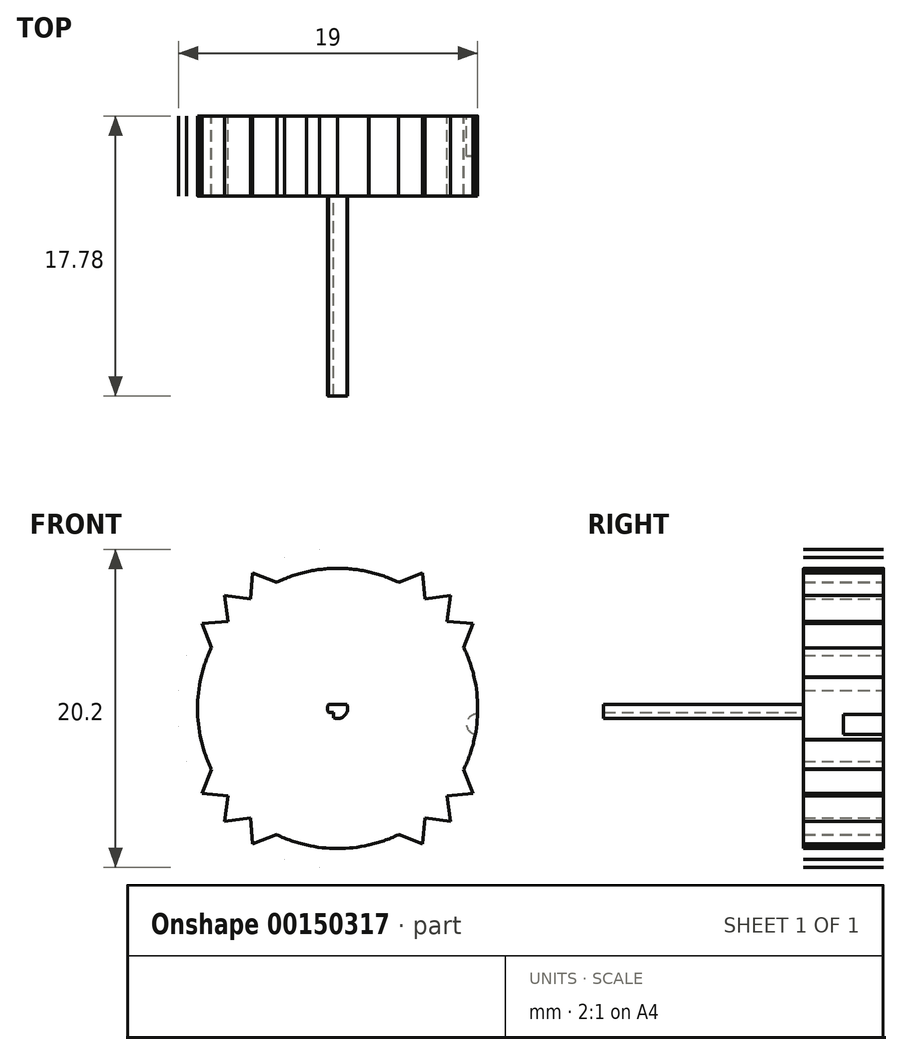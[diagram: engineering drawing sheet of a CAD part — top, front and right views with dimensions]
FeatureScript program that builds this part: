
annotation { "Feature Type Name" : "Feature", "Feature Type Description" : "" }
export const myFeature = defineFeature(function(context is Context, id is Id, definition is map)
    precondition{}
    {
        {
            var Q0;
            Q0=qCreatedBy(makeId("Front.planeOp"),FACE);
            var sketch = newSketch(context, id + "F0", { "sketchPlane" : qUnion([Q0])});
            skCircle(sketch, "E0", {"center": v(0, 0) * mm, "radius": 10.16 * mm});
            skCircle(sketch, "E1", {"center": v(0, 0) * mm, "radius": 8.9 * mm});
            skLineSegment(sketch, "E2", {"start": v(0, 0) * mm, "end": v(0, 8.9) * mm});
            skLineSegment(sketch, "E3", {"start": v(0, 8.9) * mm, "end": v(0, -8.9) * mm});
            skLineSegment(sketch, "E4", {"start": v(0, -8.9) * mm, "end": v(-1.14, -10.1) * mm});
            skLineSegment(sketch, "E5", {"start": v(-1.14, -10.1) * mm, "end": v(-1.98, -8.67) * mm});
            skLineSegment(sketch, "E6", {"start": v(-1.98, -8.67) * mm, "end": v(0, 0) * mm});
            skLineSegment(sketch, "E7", {"start": v(-1.14, -10.1) * mm, "end": v(0, 0) * mm});
            skLineSegment(sketch, "E8", {"start": v(0, 0) * mm, "end": v(-3.36, -9.59) * mm});
            skLineSegment(sketch, "E9", {"start": v(0, 0) * mm, "end": v(-3.86, -8) * mm});
            skLineSegment(sketch, "E10", {"start": v(-3.86, -8) * mm, "end": v(-3.36, -9.59) * mm});
            skLineSegment(sketch, "E11", {"start": v(-1.98, -8.67) * mm, "end": v(-3.36, -9.59) * mm});
            skLineSegment(sketch, "E12.MirrorCS", {"start": v(-3.86, -8) * mm, "end": v(-5.4, -8.6) * mm});
            skLineSegment(sketch, "E13.MirrorCS", {"start": v(0, 0) * mm, "end": v(-5.4, -8.6) * mm});
            skLineSegment(sketch, "E14.MirrorCS", {"start": v(-5.54, -6.95) * mm, "end": v(-5.4, -8.6) * mm});
            skLineSegment(sketch, "E15.MirrorCS", {"start": v(-7.18, -7.18) * mm, "end": v(-5.54, -6.95) * mm});
            skLineSegment(sketch, "E16.MirrorCS", {"start": v(-5.54, -6.95) * mm, "end": v(0, 0) * mm});
            skLineSegment(sketch, "E17.MirrorCS", {"start": v(-7.18, -7.18) * mm, "end": v(0, 0) * mm});
            skLineSegment(sketch, "E18.MirrorCS", {"start": v(-6.95, -5.54) * mm, "end": v(-7.18, -7.18) * mm});
            skLineSegment(sketch, "E19.MirrorCS", {"start": v(6.95, 5.54) * mm, "end": v(-6.95, -5.54) * mm});
            skLineSegment(sketch, "E20.MirrorCS", {"start": v(-6.95, -5.54) * mm, "end": v(-8.6, -5.4) * mm});
            skLineSegment(sketch, "E21.MirrorCS", {"start": v(-8.6, -5.4) * mm, "end": v(0, 0) * mm});
            skLineSegment(sketch, "E22.MirrorCS", {"start": v(-8.6, -5.4) * mm, "end": v(-8, -3.86) * mm});
            skLineSegment(sketch, "E23.MirrorCS", {"start": v(-8, -3.86) * mm, "end": v(0, 0) * mm});
            skLineSegment(sketch, "E24.MirrorCS", {"start": v(-8, -3.86) * mm, "end": v(-9.59, -3.36) * mm});
            skLineSegment(sketch, "E25.MirrorCS", {"start": v(0, 0) * mm, "end": v(-9.59, -3.36) * mm});
            skLineSegment(sketch, "E26.MirrorCS", {"start": v(-8.67, -1.98) * mm, "end": v(-9.59, -3.36) * mm});
            skLineSegment(sketch, "E27.MirrorCS", {"start": v(0, 0) * mm, "end": v(-8.67, -1.98) * mm});
            skLineSegment(sketch, "E28.MirrorCS", {"start": v(-8.67, -1.98) * mm, "end": v(-10.1, -1.14) * mm});
            skLineSegment(sketch, "E29.MirrorCS", {"start": v(0, 0) * mm, "end": v(-10.1, -1.14) * mm});
            skLineSegment(sketch, "E30.MirrorCS", {"start": v(-8.9, 0) * mm, "end": v(-10.1, -1.14) * mm});
            skLineSegment(sketch, "E31.MirrorCS", {"start": v(-8.9, 0) * mm, "end": v(0, 0) * mm});
            skLineSegment(sketch, "E32.MirrorCS", {"start": v(-10.1, 1.14) * mm, "end": v(-8.9, 0) * mm});
            skLineSegment(sketch, "E33.MirrorCS", {"start": v(-10.1, 1.14) * mm, "end": v(0, 0) * mm});
            skLineSegment(sketch, "E34.MirrorCS", {"start": v(-8.67, 1.98) * mm, "end": v(-10.1, 1.14) * mm});
            skLineSegment(sketch, "E35.MirrorCS", {"start": v(8.67, -1.98) * mm, "end": v(-8.67, 1.98) * mm});
            skLineSegment(sketch, "E36.MirrorCS", {"start": v(-8.67, 1.98) * mm, "end": v(-9.59, 3.36) * mm});
            skLineSegment(sketch, "E37.MirrorCS", {"start": v(-9.59, 3.36) * mm, "end": v(0, 0) * mm});
            skLineSegment(sketch, "E38.MirrorCS", {"start": v(-9.59, 3.36) * mm, "end": v(-8, 3.86) * mm});
            skLineSegment(sketch, "E39.MirrorCS", {"start": v(-8, 3.86) * mm, "end": v(0, 0) * mm});
            skLineSegment(sketch, "E40.MirrorCS", {"start": v(-8, 3.86) * mm, "end": v(-8.6, 5.4) * mm});
            skLineSegment(sketch, "E41.MirrorCS", {"start": v(0, 0) * mm, "end": v(-8.6, 5.4) * mm});
            skLineSegment(sketch, "E42.MirrorCS", {"start": v(-6.95, 5.54) * mm, "end": v(-8.6, 5.4) * mm});
            skLineSegment(sketch, "E43.MirrorCS", {"start": v(0, 0) * mm, "end": v(-6.95, 5.54) * mm});
            skLineSegment(sketch, "E44.MirrorCS", {"start": v(-6.95, 5.54) * mm, "end": v(-7.18, 7.18) * mm});
            skLineSegment(sketch, "E45.MirrorCS", {"start": v(0, 0) * mm, "end": v(-7.18, 7.18) * mm});
            skLineSegment(sketch, "E46.MirrorCS", {"start": v(-5.54, 6.95) * mm, "end": v(-7.18, 7.18) * mm});
            skLineSegment(sketch, "E47.MirrorCS", {"start": v(-5.54, 6.95) * mm, "end": v(0, 0) * mm});
            skLineSegment(sketch, "E48.MirrorCS", {"start": v(-5.4, 8.6) * mm, "end": v(-5.54, 6.95) * mm});
            skLineSegment(sketch, "E49.MirrorCS", {"start": v(-5.4, 8.6) * mm, "end": v(0, 0) * mm});
            skLineSegment(sketch, "E50.MirrorCS", {"start": v(-3.86, 8) * mm, "end": v(-5.4, 8.6) * mm});
            skLineSegment(sketch, "E51.MirrorCS", {"start": v(3.86, -8) * mm, "end": v(-3.86, 8) * mm});
            skLineSegment(sketch, "E52.MirrorCS", {"start": v(-3.86, 8) * mm, "end": v(-3.36, 9.59) * mm});
            skLineSegment(sketch, "E53.MirrorCS", {"start": v(-3.36, 9.59) * mm, "end": v(0, 0) * mm});
            skLineSegment(sketch, "E54.MirrorCS", {"start": v(-3.36, 9.59) * mm, "end": v(-1.98, 8.67) * mm});
            skLineSegment(sketch, "E55.MirrorCS", {"start": v(-1.98, 8.67) * mm, "end": v(0, 0) * mm});
            skLineSegment(sketch, "E56.MirrorCS", {"start": v(-1.98, 8.67) * mm, "end": v(-1.14, 10.1) * mm});
            skLineSegment(sketch, "E57.MirrorCS", {"start": v(0, 0) * mm, "end": v(-1.14, 10.1) * mm});
            skLineSegment(sketch, "E58.MirrorCS", {"start": v(0, 8.89) * mm, "end": v(-1.14, 10.1) * mm});
            skLineSegment(sketch, "E59.MirrorCS", {"start": v(0, 0) * mm, "end": v(0, 8.89) * mm});
            skLineSegment(sketch, "E60.MirrorCS", {"start": v(0, 8.89) * mm, "end": v(1.14, 10.1) * mm});
            skLineSegment(sketch, "E61.MirrorCS", {"start": v(0, 0) * mm, "end": v(1.14, 10.1) * mm});
            skLineSegment(sketch, "E62.MirrorCS", {"start": v(1.98, 8.67) * mm, "end": v(1.14, 10.1) * mm});
            skLineSegment(sketch, "E63.MirrorCS", {"start": v(1.98, 8.67) * mm, "end": v(0, 0) * mm});
            skLineSegment(sketch, "E64.MirrorCS", {"start": v(3.36, 9.59) * mm, "end": v(1.98, 8.67) * mm});
            skLineSegment(sketch, "E65.MirrorCS", {"start": v(3.36, 9.59) * mm, "end": v(0, 0) * mm});
            skLineSegment(sketch, "E66.MirrorCS", {"start": v(3.86, 8) * mm, "end": v(3.36, 9.59) * mm});
            skLineSegment(sketch, "E67.MirrorCS", {"start": v(-3.86, -8) * mm, "end": v(3.86, 8) * mm});
            skLineSegment(sketch, "E68.MirrorCS", {"start": v(3.86, 8) * mm, "end": v(5.4, 8.6) * mm});
            skLineSegment(sketch, "E69.MirrorCS", {"start": v(5.4, 8.6) * mm, "end": v(0, 0) * mm});
            skLineSegment(sketch, "E70.MirrorCS", {"start": v(5.4, 8.6) * mm, "end": v(5.54, 6.95) * mm});
            skLineSegment(sketch, "E71.MirrorCS", {"start": v(5.54, 6.95) * mm, "end": v(0, 0) * mm});
            skLineSegment(sketch, "E72.MirrorCS", {"start": v(5.54, 6.95) * mm, "end": v(7.18, 7.18) * mm});
            skLineSegment(sketch, "E73.MirrorCS", {"start": v(0, 0) * mm, "end": v(7.18, 7.18) * mm});
            skLineSegment(sketch, "E74.MirrorCS", {"start": v(6.95, 5.54) * mm, "end": v(7.18, 7.18) * mm});
            skLineSegment(sketch, "E75.MirrorCS", {"start": v(6.95, 5.54) * mm, "end": v(8.6, 5.4) * mm});
            skLineSegment(sketch, "E76.MirrorCS", {"start": v(0, 0) * mm, "end": v(8.6, 5.4) * mm});
            skLineSegment(sketch, "E77.MirrorCS", {"start": v(8, 3.86) * mm, "end": v(8.6, 5.4) * mm});
            skLineSegment(sketch, "E78.MirrorCS", {"start": v(8, 3.86) * mm, "end": v(0, 0) * mm});
            skLineSegment(sketch, "E79.MirrorCS", {"start": v(9.59, 3.36) * mm, "end": v(8, 3.86) * mm});
            skLineSegment(sketch, "E80.MirrorCS", {"start": v(9.59, 3.36) * mm, "end": v(0, 0) * mm});
            skLineSegment(sketch, "E81.MirrorCS", {"start": v(8.67, 1.98) * mm, "end": v(9.59, 3.36) * mm});
            skLineSegment(sketch, "E82.MirrorCS", {"start": v(-8.67, -1.98) * mm, "end": v(8.67, 1.98) * mm});
            skLineSegment(sketch, "E83.MirrorCS", {"start": v(8.67, 1.98) * mm, "end": v(10.1, 1.14) * mm});
            skLineSegment(sketch, "E84.MirrorCS", {"start": v(10.1, 1.14) * mm, "end": v(8.9, 0) * mm});
            skLineSegment(sketch, "E85.MirrorCS", {"start": v(10.1, 1.14) * mm, "end": v(0, 0) * mm});
            skLineSegment(sketch, "E86.MirrorCS", {"start": v(8.9, 0) * mm, "end": v(0, 0) * mm});
            skLineSegment(sketch, "E87.MirrorCS", {"start": v(8.9, 0) * mm, "end": v(10.1, -1.14) * mm});
            skLineSegment(sketch, "E88.MirrorCS", {"start": v(0, 0) * mm, "end": v(10.1, -1.14) * mm});
            skLineSegment(sketch, "E89.MirrorCS", {"start": v(8.67, -1.98) * mm, "end": v(10.1, -1.14) * mm});
            skLineSegment(sketch, "E90.MirrorCS", {"start": v(0, 0) * mm, "end": v(8.67, -1.98) * mm});
            skLineSegment(sketch, "E91.MirrorCS", {"start": v(8.67, -1.98) * mm, "end": v(9.59, -3.36) * mm});
            skLineSegment(sketch, "E92.MirrorCS", {"start": v(0, 0) * mm, "end": v(9.59, -3.36) * mm});
            skLineSegment(sketch, "E93.MirrorCS", {"start": v(8, -3.86) * mm, "end": v(9.59, -3.36) * mm});
            skLineSegment(sketch, "E94.MirrorCS", {"start": v(8, -3.86) * mm, "end": v(0, 0) * mm});
            skLineSegment(sketch, "E95.MirrorCS", {"start": v(8.6, -5.4) * mm, "end": v(8, -3.86) * mm});
            skLineSegment(sketch, "E96.MirrorCS", {"start": v(8.6, -5.4) * mm, "end": v(0, 0) * mm});
            skLineSegment(sketch, "E97.MirrorCS", {"start": v(6.95, -5.54) * mm, "end": v(8.6, -5.4) * mm});
            skLineSegment(sketch, "E98.MirrorCS", {"start": v(-6.95, 5.54) * mm, "end": v(6.95, -5.54) * mm});
            skLineSegment(sketch, "E99.MirrorCS", {"start": v(6.95, -5.54) * mm, "end": v(7.18, -7.18) * mm});
            skLineSegment(sketch, "E100.MirrorCS", {"start": v(7.18, -7.18) * mm, "end": v(0, 0) * mm});
            skLineSegment(sketch, "E101.MirrorCS", {"start": v(7.18, -7.18) * mm, "end": v(5.54, -6.95) * mm});
            skLineSegment(sketch, "E102.MirrorCS", {"start": v(5.54, -6.95) * mm, "end": v(0, 0) * mm});
            skLineSegment(sketch, "E103.MirrorCS", {"start": v(5.54, -6.95) * mm, "end": v(5.4, -8.6) * mm});
            skLineSegment(sketch, "E104.MirrorCS", {"start": v(0, 0) * mm, "end": v(5.4, -8.6) * mm});
            skLineSegment(sketch, "E105.MirrorCS", {"start": v(3.86, -8) * mm, "end": v(5.4, -8.6) * mm});
            skLineSegment(sketch, "E106.MirrorCS", {"start": v(0, 0) * mm, "end": v(3.86, -8) * mm});
            skLineSegment(sketch, "E107.MirrorCS", {"start": v(3.86, -8) * mm, "end": v(3.36, -9.59) * mm});
            skLineSegment(sketch, "E108.MirrorCS", {"start": v(1.98, -8.67) * mm, "end": v(3.36, -9.59) * mm});
            skLineSegment(sketch, "E109.MirrorCS", {"start": v(0, 0) * mm, "end": v(3.36, -9.59) * mm});
            skLineSegment(sketch, "E110.MirrorCS", {"start": v(1.98, -8.67) * mm, "end": v(0, 0) * mm});
            skLineSegment(sketch, "E111.MirrorCS", {"start": v(1.14, -10.1) * mm, "end": v(1.98, -8.67) * mm});
            skLineSegment(sketch, "E112.MirrorCS", {"start": v(1.14, -10.1) * mm, "end": v(0, 0) * mm});
            skLineSegment(sketch, "E113.MirrorCS", {"start": v(0, -8.9) * mm, "end": v(1.14, -10.1) * mm});
            skSolve(sketch);
        }
        {
            var Q0;
            {var subQ0=sQuery(id+"F0.wireOp",EDGE,"E51.MirrorCS");Q0=makeQuery(id+"F0.imprint","IMPRINT",FACE,{"disambiguationData":[TD([[makeQuery(id+"F0.imprint","IMPRINT",EDGE,{"derivedFrom":subQ0}),1.0]])]});}
            var Q1;
            {var subQ0=sQuery(id+"F0.wireOp",EDGE,"E47.MirrorCS");Q1=makeQuery(id+"F0.imprint","IMPRINT",FACE,{"disambiguationData":[TD([[makeQuery(id+"F0.imprint","IMPRINT",EDGE,{"derivedFrom":subQ0}),1.0]])]});}
            var Q2;
            {var subQ0=sQuery(id+"F0.wireOp",EDGE,"E48.MirrorCS");Q2=makeQuery(id+"F0.imprint","IMPRINT",FACE,{"disambiguationData":[TD([[makeQuery(id+"F0.imprint","IMPRINT",EDGE,{"derivedFrom":subQ0}),1.0]])]});}
            var Q3;
            {var subQ0=sQuery(id+"F0.wireOp",EDGE,"E50.MirrorCS");Q3=makeQuery(id+"F0.imprint","IMPRINT",FACE,{"disambiguationData":[TD([[makeQuery(id+"F0.imprint","IMPRINT",EDGE,{"derivedFrom":subQ0}),1.0]])]});}
            var Q4;
            {var subQ0=sQuery(id+"F0.wireOp",EDGE,"E52.MirrorCS");Q4=makeQuery(id+"F0.imprint","IMPRINT",FACE,{"disambiguationData":[TD([[makeQuery(id+"F0.imprint","IMPRINT",EDGE,{"derivedFrom":subQ0}),-1.0]])]});}
            var Q5;
            {var subQ0=sQuery(id+"F0.wireOp",EDGE,"E54.MirrorCS");Q5=makeQuery(id+"F0.imprint","IMPRINT",FACE,{"disambiguationData":[TD([[makeQuery(id+"F0.imprint","IMPRINT",EDGE,{"derivedFrom":subQ0}),-1.0]])]});}
            var Q6;
            {var subQ0=sQuery(id+"F0.wireOp",EDGE,"E55.MirrorCS");Q6=makeQuery(id+"F0.imprint","IMPRINT",FACE,{"disambiguationData":[TD([[makeQuery(id+"F0.imprint","IMPRINT",EDGE,{"derivedFrom":subQ0}),-1.0]])]});}
            var Q7;
            {var subQ0=sQuery(id+"F0.wireOp",EDGE,"E51.MirrorCS");Q7=makeQuery(id+"F0.imprint","IMPRINT",FACE,{"disambiguationData":[TD([[makeQuery(id+"F0.imprint","IMPRINT",EDGE,{"derivedFrom":subQ0}),-1.0]])]});}
            var Q8;
            {var subQ1=sQuery(id+"F0.wireOp",EDGE,"E1");var subQ3=sQuery(id+"F0.wireOp",EDGE,"E57.MirrorCS");var subQ4=makeQuery(id+"F0.imprint","INTERSECT",VERTEX,{"derivedFrom":[subQ1,subQ3]});Q8=makeQuery(id+"F0.imprint","IMPRINT",FACE,{"disambiguationData":[TD([[makeQuery(id+"F0.imprint","IMPRINT",EDGE,{"disambiguationData":[TD([[subQ4,1.0]])],"derivedFrom":subQ1}),1.0]])]});}
            var Q9;
            {var subQ0=sQuery(id+"F0.wireOp",EDGE,"E58.MirrorCS");Q9=makeQuery(id+"F0.imprint","IMPRINT",FACE,{"disambiguationData":[TD([[makeQuery(id+"F0.imprint","IMPRINT",EDGE,{"derivedFrom":subQ0}),1.0]])]});}
            var Q10;
            {var subQ0=sQuery(id+"F0.wireOp",EDGE,"E56.MirrorCS");Q10=makeQuery(id+"F0.imprint","IMPRINT",FACE,{"disambiguationData":[TD([[makeQuery(id+"F0.imprint","IMPRINT",EDGE,{"derivedFrom":subQ0}),-1.0]])]});}
            var Q11;
            {var subQ0=sQuery(id+"F0.wireOp",EDGE,"E55.MirrorCS");Q11=makeQuery(id+"F0.imprint","IMPRINT",FACE,{"disambiguationData":[TD([[makeQuery(id+"F0.imprint","IMPRINT",EDGE,{"derivedFrom":subQ0}),1.0]])]});}
            var Q12;
            {var subQ0=sQuery(id+"F0.wireOp",EDGE,"E47.MirrorCS");Q12=makeQuery(id+"F0.imprint","IMPRINT",FACE,{"disambiguationData":[TD([[makeQuery(id+"F0.imprint","IMPRINT",EDGE,{"derivedFrom":subQ0}),-1.0]])]});}
            var Q13;
            {var subQ0=sQuery(id+"F0.wireOp",EDGE,"E46.MirrorCS");Q13=makeQuery(id+"F0.imprint","IMPRINT",FACE,{"disambiguationData":[TD([[makeQuery(id+"F0.imprint","IMPRINT",EDGE,{"derivedFrom":subQ0}),1.0]])]});}
            var Q14;
            {var subQ1=sQuery(id+"F0.wireOp",EDGE,"E1");var subQ3=sQuery(id+"F0.wireOp",EDGE,"E45.MirrorCS");var subQ4=makeQuery(id+"F0.imprint","INTERSECT",VERTEX,{"derivedFrom":[subQ1,subQ3]});Q14=makeQuery(id+"F0.imprint","IMPRINT",FACE,{"disambiguationData":[TD([[makeQuery(id+"F0.imprint","IMPRINT",EDGE,{"disambiguationData":[TD([[subQ4,-1.0]])],"derivedFrom":subQ1}),1.0]])]});}
            var Q15;
            {var subQ0=sQuery(id+"F0.wireOp",EDGE,"E44.MirrorCS");Q15=makeQuery(id+"F0.imprint","IMPRINT",FACE,{"disambiguationData":[TD([[makeQuery(id+"F0.imprint","IMPRINT",EDGE,{"derivedFrom":subQ0}),-1.0]])]});}
            var Q16;
            {var subQ1=sQuery(id+"F0.wireOp",EDGE,"E1");var subQ3=sQuery(id+"F0.wireOp",EDGE,"E41.MirrorCS");var subQ4=makeQuery(id+"F0.imprint","INTERSECT",VERTEX,{"derivedFrom":[subQ1,subQ3]});Q16=makeQuery(id+"F0.imprint","IMPRINT",FACE,{"disambiguationData":[TD([[makeQuery(id+"F0.imprint","IMPRINT",EDGE,{"disambiguationData":[TD([[subQ4,1.0]])],"derivedFrom":subQ1}),1.0]])]});}
            var Q17;
            {var subQ0=sQuery(id+"F0.wireOp",EDGE,"E42.MirrorCS");Q17=makeQuery(id+"F0.imprint","IMPRINT",FACE,{"disambiguationData":[TD([[makeQuery(id+"F0.imprint","IMPRINT",EDGE,{"derivedFrom":subQ0}),1.0]])]});}
            var Q18;
            {var subQ0=sQuery(id+"F0.wireOp",EDGE,"E40.MirrorCS");Q18=makeQuery(id+"F0.imprint","IMPRINT",FACE,{"disambiguationData":[TD([[makeQuery(id+"F0.imprint","IMPRINT",EDGE,{"derivedFrom":subQ0}),-1.0]])]});}
            var Q19;
            {var subQ0=sQuery(id+"F0.wireOp",EDGE,"E39.MirrorCS");Q19=makeQuery(id+"F0.imprint","IMPRINT",FACE,{"disambiguationData":[TD([[makeQuery(id+"F0.imprint","IMPRINT",EDGE,{"derivedFrom":subQ0}),1.0]])]});}
            var Q20;
            {var subQ0=sQuery(id+"F0.wireOp",EDGE,"E39.MirrorCS");Q20=makeQuery(id+"F0.imprint","IMPRINT",FACE,{"disambiguationData":[TD([[makeQuery(id+"F0.imprint","IMPRINT",EDGE,{"derivedFrom":subQ0}),-1.0]])]});}
            var Q21;
            {var subQ0=sQuery(id+"F0.wireOp",EDGE,"E38.MirrorCS");Q21=makeQuery(id+"F0.imprint","IMPRINT",FACE,{"disambiguationData":[TD([[makeQuery(id+"F0.imprint","IMPRINT",EDGE,{"derivedFrom":subQ0}),-1.0]])]});}
            var Q22;
            {var subQ0=sQuery(id+"F0.wireOp",EDGE,"E36.MirrorCS");Q22=makeQuery(id+"F0.imprint","IMPRINT",FACE,{"disambiguationData":[TD([[makeQuery(id+"F0.imprint","IMPRINT",EDGE,{"derivedFrom":subQ0}),-1.0]])]});}
            var Q23;
            {var subQ0=sQuery(id+"F0.wireOp",EDGE,"E35.MirrorCS");Q23=makeQuery(id+"F0.imprint","IMPRINT",FACE,{"disambiguationData":[TD([[makeQuery(id+"F0.imprint","IMPRINT",EDGE,{"derivedFrom":subQ0}),-1.0]])]});}
            var Q24;
            {var subQ0=sQuery(id+"F0.wireOp",EDGE,"E35.MirrorCS");Q24=makeQuery(id+"F0.imprint","IMPRINT",FACE,{"disambiguationData":[TD([[makeQuery(id+"F0.imprint","IMPRINT",EDGE,{"derivedFrom":subQ0}),1.0]])]});}
            var Q25;
            {var subQ0=sQuery(id+"F0.wireOp",EDGE,"E34.MirrorCS");Q25=makeQuery(id+"F0.imprint","IMPRINT",FACE,{"disambiguationData":[TD([[makeQuery(id+"F0.imprint","IMPRINT",EDGE,{"derivedFrom":subQ0}),1.0]])]});}
            var Q26;
            {var subQ0=sQuery(id+"F0.wireOp",EDGE,"E32.MirrorCS");Q26=makeQuery(id+"F0.imprint","IMPRINT",FACE,{"disambiguationData":[TD([[makeQuery(id+"F0.imprint","IMPRINT",EDGE,{"derivedFrom":subQ0}),1.0]])]});}
            var Q27;
            {var subQ0=sQuery(id+"F0.wireOp",EDGE,"E31.MirrorCS");Q27=makeQuery(id+"F0.imprint","IMPRINT",FACE,{"disambiguationData":[TD([[makeQuery(id+"F0.imprint","IMPRINT",EDGE,{"derivedFrom":subQ0}),1.0]])]});}
            var Q28;
            {var subQ0=sQuery(id+"F0.wireOp",EDGE,"E31.MirrorCS");Q28=makeQuery(id+"F0.imprint","IMPRINT",FACE,{"disambiguationData":[TD([[makeQuery(id+"F0.imprint","IMPRINT",EDGE,{"derivedFrom":subQ0}),-1.0]])]});}
            var Q29;
            {var subQ0=sQuery(id+"F0.wireOp",EDGE,"E30.MirrorCS");Q29=makeQuery(id+"F0.imprint","IMPRINT",FACE,{"disambiguationData":[TD([[makeQuery(id+"F0.imprint","IMPRINT",EDGE,{"derivedFrom":subQ0}),1.0]])]});}
            var Q30;
            {var subQ0=sQuery(id+"F0.wireOp",EDGE,"E28.MirrorCS");Q30=makeQuery(id+"F0.imprint","IMPRINT",FACE,{"disambiguationData":[TD([[makeQuery(id+"F0.imprint","IMPRINT",EDGE,{"derivedFrom":subQ0}),-1.0]])]});}
            var Q31;
            {var subQ1=sQuery(id+"F0.wireOp",EDGE,"E1");var subQ3=sQuery(id+"F0.wireOp",EDGE,"E29.MirrorCS");var subQ4=makeQuery(id+"F0.imprint","INTERSECT",VERTEX,{"derivedFrom":[subQ1,subQ3]});Q31=makeQuery(id+"F0.imprint","IMPRINT",FACE,{"disambiguationData":[TD([[makeQuery(id+"F0.imprint","IMPRINT",EDGE,{"disambiguationData":[TD([[subQ4,-1.0]])],"derivedFrom":subQ1}),1.0]])]});}
            var Q32;
            {var subQ1=sQuery(id+"F0.wireOp",EDGE,"E1");var subQ3=sQuery(id+"F0.wireOp",EDGE,"E25.MirrorCS");var subQ4=makeQuery(id+"F0.imprint","INTERSECT",VERTEX,{"derivedFrom":[subQ1,subQ3]});Q32=makeQuery(id+"F0.imprint","IMPRINT",FACE,{"disambiguationData":[TD([[makeQuery(id+"F0.imprint","IMPRINT",EDGE,{"disambiguationData":[TD([[subQ4,1.0]])],"derivedFrom":subQ1}),1.0]])]});}
            var Q33;
            {var subQ0=sQuery(id+"F0.wireOp",EDGE,"E26.MirrorCS");Q33=makeQuery(id+"F0.imprint","IMPRINT",FACE,{"disambiguationData":[TD([[makeQuery(id+"F0.imprint","IMPRINT",EDGE,{"derivedFrom":subQ0}),1.0]])]});}
            var Q34;
            {var subQ0=sQuery(id+"F0.wireOp",EDGE,"E24.MirrorCS");Q34=makeQuery(id+"F0.imprint","IMPRINT",FACE,{"disambiguationData":[TD([[makeQuery(id+"F0.imprint","IMPRINT",EDGE,{"derivedFrom":subQ0}),-1.0]])]});}
            var Q35;
            {var subQ0=sQuery(id+"F0.wireOp",EDGE,"E23.MirrorCS");Q35=makeQuery(id+"F0.imprint","IMPRINT",FACE,{"disambiguationData":[TD([[makeQuery(id+"F0.imprint","IMPRINT",EDGE,{"derivedFrom":subQ0}),1.0]])]});}
            var Q36;
            {var subQ0=sQuery(id+"F0.wireOp",EDGE,"E23.MirrorCS");Q36=makeQuery(id+"F0.imprint","IMPRINT",FACE,{"disambiguationData":[TD([[makeQuery(id+"F0.imprint","IMPRINT",EDGE,{"derivedFrom":subQ0}),-1.0]])]});}
            var Q37;
            {var subQ0=sQuery(id+"F0.wireOp",EDGE,"E22.MirrorCS");Q37=makeQuery(id+"F0.imprint","IMPRINT",FACE,{"disambiguationData":[TD([[makeQuery(id+"F0.imprint","IMPRINT",EDGE,{"derivedFrom":subQ0}),-1.0]])]});}
            var Q38;
            {var subQ0=sQuery(id+"F0.wireOp",EDGE,"E20.MirrorCS");Q38=makeQuery(id+"F0.imprint","IMPRINT",FACE,{"disambiguationData":[TD([[makeQuery(id+"F0.imprint","IMPRINT",EDGE,{"derivedFrom":subQ0}),-1.0]])]});}
            var Q39;
            {var subQ1=sQuery(id+"F0.wireOp",EDGE,"E1");var subQ3=sQuery(id+"F0.wireOp",EDGE,"E21.MirrorCS");var subQ4=makeQuery(id+"F0.imprint","INTERSECT",VERTEX,{"derivedFrom":[subQ1,subQ3]});Q39=makeQuery(id+"F0.imprint","IMPRINT",FACE,{"disambiguationData":[TD([[makeQuery(id+"F0.imprint","IMPRINT",EDGE,{"disambiguationData":[TD([[subQ4,-1.0]])],"derivedFrom":subQ1}),1.0]])]});}
            var Q40;
            {var subQ1=sQuery(id+"F0.wireOp",EDGE,"E1");var subQ3=sQuery(id+"F0.wireOp",EDGE,"E17.MirrorCS");var subQ4=makeQuery(id+"F0.imprint","INTERSECT",VERTEX,{"derivedFrom":[subQ1,subQ3]});Q40=makeQuery(id+"F0.imprint","IMPRINT",FACE,{"disambiguationData":[TD([[makeQuery(id+"F0.imprint","IMPRINT",EDGE,{"disambiguationData":[TD([[subQ4,1.0]])],"derivedFrom":subQ1}),1.0]])]});}
            var Q41;
            {var subQ0=sQuery(id+"F0.wireOp",EDGE,"E16.MirrorCS");Q41=makeQuery(id+"F0.imprint","IMPRINT",FACE,{"disambiguationData":[TD([[makeQuery(id+"F0.imprint","IMPRINT",EDGE,{"derivedFrom":subQ0}),1.0]])]});}
            var Q42;
            {var subQ0=sQuery(id+"F0.wireOp",EDGE,"E16.MirrorCS");Q42=makeQuery(id+"F0.imprint","IMPRINT",FACE,{"disambiguationData":[TD([[makeQuery(id+"F0.imprint","IMPRINT",EDGE,{"derivedFrom":subQ0}),-1.0]])]});}
            var Q43;
            {var subQ0=sQuery(id+"F0.wireOp",EDGE,"E18.MirrorCS");Q43=makeQuery(id+"F0.imprint","IMPRINT",FACE,{"disambiguationData":[TD([[makeQuery(id+"F0.imprint","IMPRINT",EDGE,{"derivedFrom":subQ0}),1.0]])]});}
            var Q44;
            {var subQ0=sQuery(id+"F0.wireOp",EDGE,"E15.MirrorCS");Q44=makeQuery(id+"F0.imprint","IMPRINT",FACE,{"disambiguationData":[TD([[makeQuery(id+"F0.imprint","IMPRINT",EDGE,{"derivedFrom":subQ0}),1.0]])]});}
            var Q45;
            {var subQ0=sQuery(id+"F0.wireOp",EDGE,"E14.MirrorCS");Q45=makeQuery(id+"F0.imprint","IMPRINT",FACE,{"disambiguationData":[TD([[makeQuery(id+"F0.imprint","IMPRINT",EDGE,{"derivedFrom":subQ0}),1.0]])]});}
            var Q46;
            {var subQ0=sQuery(id+"F0.wireOp",EDGE,"E12.MirrorCS");Q46=makeQuery(id+"F0.imprint","IMPRINT",FACE,{"disambiguationData":[TD([[makeQuery(id+"F0.imprint","IMPRINT",EDGE,{"derivedFrom":subQ0}),-1.0]])]});}
            var Q47;
            {var subQ1=sQuery(id+"F0.wireOp",EDGE,"E1");var subQ3=sQuery(id+"F0.wireOp",EDGE,"E8");var subQ4=makeQuery(id+"F0.imprint","INTERSECT",VERTEX,{"derivedFrom":[subQ1,subQ3]});Q47=makeQuery(id+"F0.imprint","IMPRINT",FACE,{"disambiguationData":[TD([[makeQuery(id+"F0.imprint","IMPRINT",EDGE,{"disambiguationData":[TD([[subQ4,1.0]])],"derivedFrom":subQ1}),1.0]])]});}
            var Q48;
            {var subQ0=sQuery(id+"F0.wireOp",EDGE,"E10");Q48=makeQuery(id+"F0.imprint","IMPRINT",FACE,{"disambiguationData":[TD([[makeQuery(id+"F0.imprint","IMPRINT",EDGE,{"derivedFrom":subQ0}),1.0]])]});}
            var Q49;
            {var subQ0=sQuery(id+"F0.wireOp",EDGE,"E11");Q49=makeQuery(id+"F0.imprint","IMPRINT",FACE,{"disambiguationData":[TD([[makeQuery(id+"F0.imprint","IMPRINT",EDGE,{"derivedFrom":subQ0}),-1.0]])]});}
            var Q50;
            {var subQ0=sQuery(id+"F0.wireOp",EDGE,"E6");Q50=makeQuery(id+"F0.imprint","IMPRINT",FACE,{"disambiguationData":[TD([[makeQuery(id+"F0.imprint","IMPRINT",EDGE,{"derivedFrom":subQ0}),1.0]])]});}
            var Q51;
            {var subQ0=sQuery(id+"F0.wireOp",EDGE,"E6");Q51=makeQuery(id+"F0.imprint","IMPRINT",FACE,{"disambiguationData":[TD([[makeQuery(id+"F0.imprint","IMPRINT",EDGE,{"derivedFrom":subQ0}),-1.0]])]});}
            var Q52;
            {var subQ0=sQuery(id+"F0.wireOp",EDGE,"E4");Q52=makeQuery(id+"F0.imprint","IMPRINT",FACE,{"disambiguationData":[TD([[makeQuery(id+"F0.imprint","IMPRINT",EDGE,{"derivedFrom":subQ0}),-1.0]])]});}
            var Q53;
            {var subQ0=sQuery(id+"F0.wireOp",EDGE,"E5");Q53=makeQuery(id+"F0.imprint","IMPRINT",FACE,{"disambiguationData":[TD([[makeQuery(id+"F0.imprint","IMPRINT",EDGE,{"derivedFrom":subQ0}),-1.0]])]});}
            var Q54;
            {var subQ1=sQuery(id+"F0.wireOp",EDGE,"E1");var subQ3=sQuery(id+"F0.wireOp",EDGE,"E7");var subQ4=makeQuery(id+"F0.imprint","INTERSECT",VERTEX,{"derivedFrom":[subQ1,subQ3]});Q54=makeQuery(id+"F0.imprint","IMPRINT",FACE,{"disambiguationData":[TD([[makeQuery(id+"F0.imprint","IMPRINT",EDGE,{"disambiguationData":[TD([[subQ4,-1.0]])],"derivedFrom":subQ1}),1.0]])]});}
            var Q55;
            {var subQ1=sQuery(id+"F0.wireOp",EDGE,"E1");var subQ3=sQuery(id+"F0.wireOp",EDGE,"E13.MirrorCS");var subQ4=makeQuery(id+"F0.imprint","INTERSECT",VERTEX,{"derivedFrom":[subQ1,subQ3]});Q55=makeQuery(id+"F0.imprint","IMPRINT",FACE,{"disambiguationData":[TD([[makeQuery(id+"F0.imprint","IMPRINT",EDGE,{"disambiguationData":[TD([[subQ4,-1.0]])],"derivedFrom":subQ1}),1.0]])]});}
            extrude(context, id + "F1", {"entities" : qUnion([Q0, Q1, Q2, Q3, Q4, Q5, Q6, Q7, Q8, Q9, Q10, Q11, Q12, Q13, Q14, Q15, Q16, Q17, Q18, Q19, Q20, Q21, Q22, Q23, Q24, Q25, Q26, Q27, Q28, Q29, Q30, Q31, Q32, Q33, Q34, Q35, Q36, Q37, Q38, Q39, Q40, Q41, Q42, Q43, Q44, Q45, Q46, Q47, Q48, Q49, Q50, Q51, Q52, Q53, Q54, Q55]), "depth" : 5.08 * mm});
        }
        {
            var Q0;
            Q0=makeQuery(id+"F1.opExtrude","SWEPT_BODY",BODY,{"disambiguationData":[OSD([sQuery(id+"F0.wireOp",EDGE,"E4"),sQuery(id+"F0.wireOp",EDGE,"E5"),sQuery(id+"F0.wireOp",EDGE,"E10"),sQuery(id+"F0.wireOp",EDGE,"E11"),sQuery(id+"F0.wireOp",EDGE,"E12.MirrorCS"),sQuery(id+"F0.wireOp",EDGE,"E14.MirrorCS"),sQuery(id+"F0.wireOp",EDGE,"E15.MirrorCS"),sQuery(id+"F0.wireOp",EDGE,"E18.MirrorCS"),sQuery(id+"F0.wireOp",EDGE,"E20.MirrorCS"),sQuery(id+"F0.wireOp",EDGE,"E22.MirrorCS"),sQuery(id+"F0.wireOp",EDGE,"E24.MirrorCS"),sQuery(id+"F0.wireOp",EDGE,"E26.MirrorCS"),sQuery(id+"F0.wireOp",EDGE,"E28.MirrorCS"),sQuery(id+"F0.wireOp",EDGE,"E30.MirrorCS"),sQuery(id+"F0.wireOp",EDGE,"E32.MirrorCS"),sQuery(id+"F0.wireOp",EDGE,"E34.MirrorCS"),sQuery(id+"F0.wireOp",EDGE,"E36.MirrorCS"),sQuery(id+"F0.wireOp",EDGE,"E38.MirrorCS"),sQuery(id+"F0.wireOp",EDGE,"E40.MirrorCS"),sQuery(id+"F0.wireOp",EDGE,"E42.MirrorCS"),sQuery(id+"F0.wireOp",EDGE,"E44.MirrorCS"),sQuery(id+"F0.wireOp",EDGE,"E46.MirrorCS"),sQuery(id+"F0.wireOp",EDGE,"E48.MirrorCS"),sQuery(id+"F0.wireOp",EDGE,"E50.MirrorCS"),sQuery(id+"F0.wireOp",EDGE,"E52.MirrorCS"),sQuery(id+"F0.wireOp",EDGE,"E54.MirrorCS"),sQuery(id+"F0.wireOp",EDGE,"E56.MirrorCS"),sQuery(id+"F0.wireOp",EDGE,"E58.MirrorCS"),sQuery(id+"F0.wireOp",EDGE,"E3")])]});
            var Q1;
            Q1=qCreatedBy(makeId("Right.planeOp"),FACE);
            mirror(context, id + "F2", {"operationType" : NewBodyOperationType.ADD, "entities" : qUnion([Q0]), "mirrorPlane" : qUnion([Q1])});
        }
        {
            var Q0;
            {var subQ0=makeQuery(id+"F1.opExtrude","CAP_FACE",FACE,{"disambiguationData":[OSD([sQuery(id+"F0.wireOp",EDGE,"E4"),sQuery(id+"F0.wireOp",EDGE,"E5"),sQuery(id+"F0.wireOp",EDGE,"E10"),sQuery(id+"F0.wireOp",EDGE,"E11"),sQuery(id+"F0.wireOp",EDGE,"E12.MirrorCS"),sQuery(id+"F0.wireOp",EDGE,"E14.MirrorCS"),sQuery(id+"F0.wireOp",EDGE,"E15.MirrorCS"),sQuery(id+"F0.wireOp",EDGE,"E18.MirrorCS"),sQuery(id+"F0.wireOp",EDGE,"E20.MirrorCS"),sQuery(id+"F0.wireOp",EDGE,"E22.MirrorCS"),sQuery(id+"F0.wireOp",EDGE,"E24.MirrorCS"),sQuery(id+"F0.wireOp",EDGE,"E26.MirrorCS"),sQuery(id+"F0.wireOp",EDGE,"E28.MirrorCS"),sQuery(id+"F0.wireOp",EDGE,"E30.MirrorCS"),sQuery(id+"F0.wireOp",EDGE,"E32.MirrorCS"),sQuery(id+"F0.wireOp",EDGE,"E34.MirrorCS"),sQuery(id+"F0.wireOp",EDGE,"E36.MirrorCS"),sQuery(id+"F0.wireOp",EDGE,"E38.MirrorCS"),sQuery(id+"F0.wireOp",EDGE,"E40.MirrorCS"),sQuery(id+"F0.wireOp",EDGE,"E42.MirrorCS"),sQuery(id+"F0.wireOp",EDGE,"E44.MirrorCS"),sQuery(id+"F0.wireOp",EDGE,"E46.MirrorCS"),sQuery(id+"F0.wireOp",EDGE,"E48.MirrorCS"),sQuery(id+"F0.wireOp",EDGE,"E50.MirrorCS"),sQuery(id+"F0.wireOp",EDGE,"E52.MirrorCS"),sQuery(id+"F0.wireOp",EDGE,"E54.MirrorCS"),sQuery(id+"F0.wireOp",EDGE,"E56.MirrorCS"),sQuery(id+"F0.wireOp",EDGE,"E58.MirrorCS"),sQuery(id+"F0.wireOp",EDGE,"E3")])],"isStart":false});Q0=makeQuery(id+"F2.boolean.opBoolean","MERGE",FACE,{"derivedFrom":[subQ0,makeQuery(id+"F2.opPattern","COPY",FACE,{"derivedFrom":subQ0,"instanceName":"1"})]});}
            var sketch = newSketch(context, id + "F3", { "sketchPlane" : qUnion([Q0])});
            skCircle(sketch, "E114", {"center": v(0, 0) * mm, "radius": 0.64 * mm});
            skLineSegment(sketch, "E115.bottom", {"start": v(1.18, 0.25) * mm, "end": v(-1.18, 0.25) * mm});
            skLineSegment(sketch, "E115.top", {"start": v(1.18, -0.25) * mm, "end": v(-1.18, -0.25) * mm});
            skLineSegment(sketch, "E115.left", {"start": v(1.18, 0.25) * mm, "end": v(1.18, -0.25) * mm});
            skLineSegment(sketch, "E115.right", {"start": v(-1.18, 0.25) * mm, "end": v(-1.18, -0.25) * mm});
            skLineSegment(sketch, "E116.bottom", {"start": v(0.25, 1.07) * mm, "end": v(-0.25, 1.07) * mm});
            skLineSegment(sketch, "E116.top", {"start": v(0.25, -1.07) * mm, "end": v(-0.25, -1.07) * mm});
            skLineSegment(sketch, "E116.left", {"start": v(0.25, 1.07) * mm, "end": v(0.25, -1.07) * mm});
            skLineSegment(sketch, "E116.right", {"start": v(-0.25, 1.07) * mm, "end": v(-0.25, -1.07) * mm});
            skSolve(sketch);
        }
        {
            var Q0;
            {var subQ0=sQuery(id+"F3.wireOp",EDGE,"E116.left");var subQ1=sQuery(id+"F3.wireOp",EDGE,"E114");var subQ2=makeQuery(id+"F3.imprint","INTERSECT",VERTEX,{"disambiguationData":[OD(0.0)],"derivedFrom":[subQ1,subQ0]});Q0=makeQuery(id+"F3.imprint","IMPRINT",FACE,{"disambiguationData":[TD([[makeQuery(id+"F3.imprint","IMPRINT",EDGE,{"disambiguationData":[TD([[subQ2,-1.0]])],"derivedFrom":subQ1}),1.0]])]});}
            var Q1;
            {var subQ0=sQuery(id+"F3.wireOp",EDGE,"E115.bottom");var subQ1=sQuery(id+"F3.wireOp",EDGE,"E114");var subQ2=makeQuery(id+"F3.imprint","INTERSECT",VERTEX,{"disambiguationData":[OD(1.0)],"derivedFrom":[subQ1,subQ0]});Q1=makeQuery(id+"F3.imprint","IMPRINT",FACE,{"disambiguationData":[TD([[makeQuery(id+"F3.imprint","IMPRINT",EDGE,{"disambiguationData":[TD([[subQ2,-1.0]])],"derivedFrom":subQ1}),1.0]])]});}
            var Q2;
            {var subQ0=sQuery(id+"F3.wireOp",EDGE,"E116.left");var subQ1=sQuery(id+"F3.wireOp",EDGE,"E115.bottom");var subQ2=makeQuery(id+"F3.imprint","INTERSECT",VERTEX,{"derivedFrom":[subQ1,subQ0]});Q2=makeQuery(id+"F3.imprint","IMPRINT",FACE,{"disambiguationData":[TD([[makeQuery(id+"F3.imprint","IMPRINT",EDGE,{"disambiguationData":[TD([[subQ2,-1.0]])],"derivedFrom":subQ1}),1.0]])]});}
            var Q3;
            {var subQ0=sQuery(id+"F3.wireOp",EDGE,"E115.bottom");var subQ1=sQuery(id+"F3.wireOp",EDGE,"E114");var subQ2=makeQuery(id+"F3.imprint","INTERSECT",VERTEX,{"disambiguationData":[OD(0.0)],"derivedFrom":[subQ1,subQ0]});Q3=makeQuery(id+"F3.imprint","IMPRINT",FACE,{"disambiguationData":[TD([[makeQuery(id+"F3.imprint","IMPRINT",EDGE,{"disambiguationData":[TD([[subQ2,1.0]])],"derivedFrom":subQ1}),1.0]])]});}
            var Q4;
            {var subQ0=sQuery(id+"F3.wireOp",EDGE,"E116.right");var subQ1=sQuery(id+"F3.wireOp",EDGE,"E114");var subQ2=makeQuery(id+"F3.imprint","INTERSECT",VERTEX,{"disambiguationData":[OD(1.0)],"derivedFrom":[subQ1,subQ0]});Q4=makeQuery(id+"F3.imprint","IMPRINT",FACE,{"disambiguationData":[TD([[makeQuery(id+"F3.imprint","IMPRINT",EDGE,{"disambiguationData":[TD([[subQ2,-1.0]])],"derivedFrom":subQ1}),1.0]])]});}
            extrude(context, id + "F4", {"entities" : qUnion([Q0, Q1, Q2, Q3, Q4]), "operationType" : NewBodyOperationType.ADD, "depth" : 12.7 * mm});
        }
        {
            var Q0;
            {var subQ0=makeQuery(id+"F1.opExtrude","CAP_FACE",FACE,{"disambiguationData":[OSD([sQuery(id+"F0.wireOp",EDGE,"E4"),sQuery(id+"F0.wireOp",EDGE,"E5"),sQuery(id+"F0.wireOp",EDGE,"E10"),sQuery(id+"F0.wireOp",EDGE,"E11"),sQuery(id+"F0.wireOp",EDGE,"E12.MirrorCS"),sQuery(id+"F0.wireOp",EDGE,"E14.MirrorCS"),sQuery(id+"F0.wireOp",EDGE,"E15.MirrorCS"),sQuery(id+"F0.wireOp",EDGE,"E18.MirrorCS"),sQuery(id+"F0.wireOp",EDGE,"E20.MirrorCS"),sQuery(id+"F0.wireOp",EDGE,"E22.MirrorCS"),sQuery(id+"F0.wireOp",EDGE,"E24.MirrorCS"),sQuery(id+"F0.wireOp",EDGE,"E26.MirrorCS"),sQuery(id+"F0.wireOp",EDGE,"E28.MirrorCS"),sQuery(id+"F0.wireOp",EDGE,"E30.MirrorCS"),sQuery(id+"F0.wireOp",EDGE,"E32.MirrorCS"),sQuery(id+"F0.wireOp",EDGE,"E34.MirrorCS"),sQuery(id+"F0.wireOp",EDGE,"E36.MirrorCS"),sQuery(id+"F0.wireOp",EDGE,"E38.MirrorCS"),sQuery(id+"F0.wireOp",EDGE,"E40.MirrorCS"),sQuery(id+"F0.wireOp",EDGE,"E42.MirrorCS"),sQuery(id+"F0.wireOp",EDGE,"E44.MirrorCS"),sQuery(id+"F0.wireOp",EDGE,"E46.MirrorCS"),sQuery(id+"F0.wireOp",EDGE,"E48.MirrorCS"),sQuery(id+"F0.wireOp",EDGE,"E50.MirrorCS"),sQuery(id+"F0.wireOp",EDGE,"E52.MirrorCS"),sQuery(id+"F0.wireOp",EDGE,"E54.MirrorCS"),sQuery(id+"F0.wireOp",EDGE,"E56.MirrorCS"),sQuery(id+"F0.wireOp",EDGE,"E58.MirrorCS"),sQuery(id+"F0.wireOp",EDGE,"E3")])],"isStart":true});Q0=makeQuery(id+"F2.boolean.opBoolean","MERGE",FACE,{"derivedFrom":[subQ0,makeQuery(id+"F2.opPattern","COPY",FACE,{"derivedFrom":subQ0,"instanceName":"1"})]});}
            var sketch = newSketch(context, id + "F5", { "sketchPlane" : qUnion([Q0])});
            skLineSegment(sketch, "E117", {"start": v(-8.9, 0) * mm, "end": v(0, 0) * mm});
            skLineSegment(sketch, "E118", {"start": v(0, 0) * mm, "end": v(-8.83, -1) * mm});
            skCircle(sketch, "E119", {"center": v(-8.83, -1) * mm, "radius": 0.64 * mm});
            skSolve(sketch);
        }
        {
            var Q0;
            Q0 = qSketchRegion(id + "F5", true);
            extrude(context, id + "F6", {"entities" : qUnion([Q0]), "operationType" : NewBodyOperationType.REMOVE, "oppositeDirection" : true, "depth" : 2.54 * mm});
        }
    });
